# Revit family: Doors_Swing_Avanti_Systems_Acoustic-Dbl-Glazed
name_source: partatom
category: Doors
revit_build: Autodesk Revit Architecture 2015 (Build: 20140606_1530(x64)
units: mm (PartAtom-declared; Revit-internal decimal feet)

## types (1)
- Double Glazed Acoustic Swing Door
    Acoustic performance (dB) = 43
    Analytic Construction = <None>
    BIMobject category = Swing
    BIMobject category code = doors-swing
    BIMobject main category = Doors
    BIMobject main category code = doors
    Brand url = http://www.avantisystemsusa.com
    Clear Anodic Finish = AAMA 611, AA-M12c22A31, Class II, 0.01mm or thicker
    Description = Double Glazed Acoustic Swing Doors fit seamlessly into the Solare™ Double Glazed, Elevare™ Stacking Double Glazed High Wall , Movare™ Movable Double Glazed or Transverto™ MonobIock Modular for superior sound resistance and style.
    Design country = United States
    Doors panel material = Glass - Avanti - Laminated Glass
    Edition number = 1
    Function = Interior
    Glass Marker = Yes
    Handle Distance = 0' - 4 1/8"
    IFC Classification = Door
    Manufacturer = Avanti Systems USA
    Manufacturer name = Avanti Systems
    Masterformat 2014 Code = 08 14 00
    Masterformat 2014 Description = Wood Doors
    Material main = Glass
    Material secondary = Aluminium
    Model = Acoustic Double Glazed Glass Swing Door
    Nominal height = 0' - 0"
    Nominal width = 0' - 0"
    OmniClass Code = 23-17 11 15
    OmniClass Description = Wood Doors
    Power = 110 V
    Product Guid = 4cbc50b4-6a02-4c5a-a436-d6565afaf1f2
    Product SKU = avanti-acoustic-double-glazed-glass-swing-door
    Product data url = https://bimobject.com
    Product family = Pivot & Hinged Doors
    Product group = Acoustic Double Glazed
    Product url = https://www.avantisystemsusa.com
    QR code = http://bimobject.com
    Sound Rating = 0
    Thickness = 0' - 1 3/4"
    UNSPSC Code = 30171504
    URL = https://www.avantisystemsusa.com
    Uniclass 1.4 Code = JL20
    Uniclass 1.4 Description = Doors
    Uniclass 2015 Code = EF_25_30
    Uniclass 2015 Name = Doors and windows
    Uniformat II Code = C1020
    Uniformat II Description = Interior Doors
    Warranty = 1 year
    Weight Net (Kg) = 0

## geometry (parser evidence)
native form markers: Sweep x19
no freeform markers — native parametric forms only
